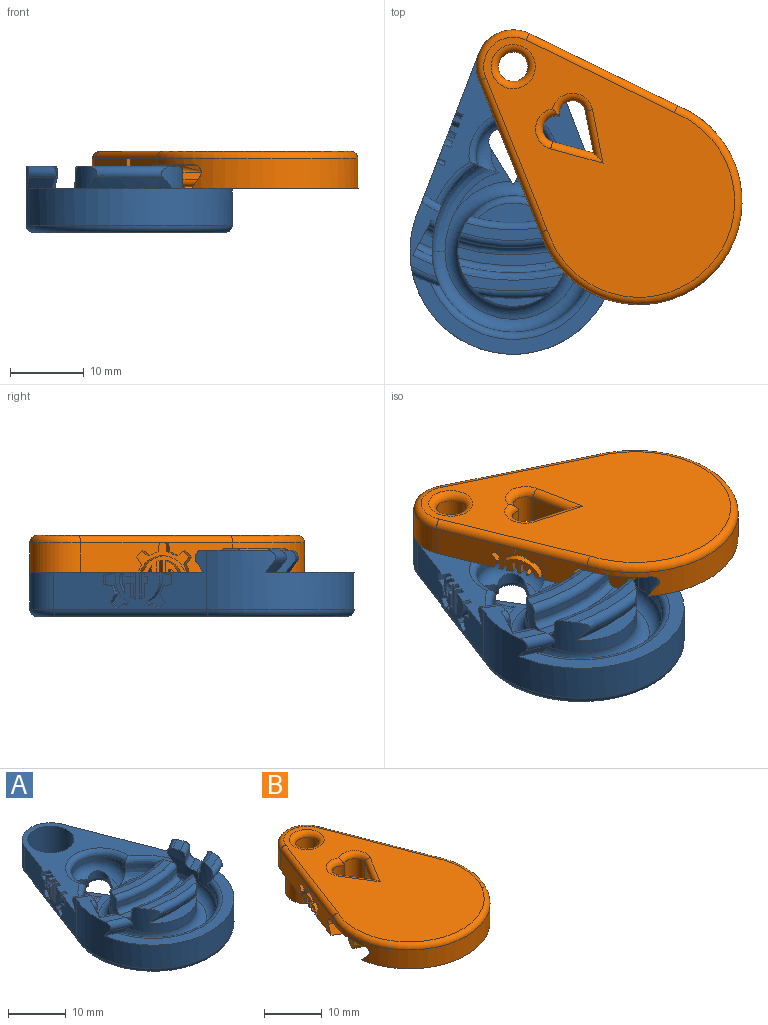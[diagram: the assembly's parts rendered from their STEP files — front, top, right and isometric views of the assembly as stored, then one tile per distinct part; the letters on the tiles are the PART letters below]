
ASSEMBLY  parts=2 mates=1
PART A: 126 faces, bbox 30.3x45.6x9 mm
  f0: plane 24.91x24.4mm, normal (0,0,1), area 152.9mm2, adj f1,f2,f3,f4,f16,f18,f20,f22
  f1: plane 6x5mm, normal (-0.93,0.36,0), area 17.6mm2, adj f0,f32,f88,f89,f90,f93,f95,f96
  f2: plane 8.53x5mm, normal (-0.93,0.36,0), area 40.9mm2, adj f0,f20,f32,f82,f83,f84,f85,f86
  f3: plane 8.01x6.52mm, normal (-0.93,0.36,0), area 34mm2, adj f0,f13,f18,f21,f32,f71,f99,f100
  f4: plane 0.75x0.53mm, normal (-0.93,0.36,0), area 0.4mm2, adj f0,f115,f116,f117
  f5: plane 0.2x0.15mm, normal (0,0,1), area 0mm2, adj f44,f74,f75
  f6: plane 8.32x7.53mm, normal (0,0,1), area 9.5mm2, adj f41,f43,f44,f76
  f7: plane 2.91x2.76mm, normal (0,0,1), area 4mm2, adj f11,f21,f22,f57,f69
  f8: plane 14.14x2.39mm, normal (0,0,1), area 19.7mm2, adj f28,f58,f73
  f9: cylinder r=11mm len=22mm, axis (0,0,-1), area 62.6mm2, adj f10,f11,f12,f13,f14,f15,f39,f42
  f10: extruded ~11.62x6.18mm, area 27.9mm2, adj f9,f13,f18,f25,f36,f41,f52,f53
  f11: extruded ~11.62x6.18mm, area 27.9mm2, adj f7,f9,f16,f25,f38,f45,f49,f50
  f12: plane 3.59x3.19mm, normal (0,0,1), area 5.2mm2, adj f9,f21,f61,f68
  f13: plane 10.21x3.95mm, normal (0,0,1), area 17.1mm2, adj f3,f9,f10,f21,f55,f56,f62,f70
  f14: cone r=32.35mm half-angle=33.7deg, axis (0,0,1), area 7.1mm2, adj f9,f21,f26,f39,f70
  f15: cone r=32.35mm half-angle=33.7deg, axis (0,0,1), area 7.1mm2, adj f9,f21,f26,f39,f68
  f16: cone r=20.36mm half-angle=33.7deg, axis (0,0,-1), area 5.4mm2, adj f0,f11,f22,f38,f69
  f17: plane 13.59x2.23mm, normal (0,0,1), area 18.1mm2, adj f28,f63,f72
  f18: cone r=20.36mm half-angle=33.7deg, axis (0,0,-1), area 5.4mm2, adj f0,f3,f10,f36,f71
  f19: plane 11.06x3.78mm, normal (0,0,1), area 29.3mm2, adj f31,f40
  f20: cylinder r=5mm len=9.34mm, axis (0,0,1), area 60.2mm2, adj f0,f2,f22,f34
  f21: cylinder r=14mm len=28mm, axis (0,0,1), area 324.8mm2, adj f3,f7,f12,f13,f14,f15,f22,f26
  f22: plane 20.87x8.02mm, normal (0.93,0.36,0), area 115.9mm2, adj f0,f7,f16,f20,f21,f35,f69
  f23: cylinder r=4mm len=8mm, axis (0,0,1), area 150.8mm2, adj f0,f24,f34
  f24: plane 39.43x26mm, normal (0,0,-1), area 635.6mm2, adj f23,f32,f33,f35,f78,f79,f80,f81
  f25: cylinder r=5mm len=10mm, axis (0,0,-1), area 18.4mm2, adj f10,f11,f37,f44
  f26: plane 27.74x12.08mm, normal (0,0,1), area 71.8mm2, adj f14,f15,f21,f39
  f27: plane 8.32x7.53mm, normal (0,0,1), area 9.5mm2, adj f43,f44,f45,f77
  f28: cylinder r=7.5mm len=15mm, axis (0,0,-1), area 122.1mm2, adj f8,f17,f29,f30,f31,f40,f43,f46
  f29: plane 11.68x2.8mm, normal (0,0,1), area 18.3mm2, adj f28,f30
  f30: cone r=32.35mm half-angle=33.7deg, axis (0,0,1), area 18.3mm2, adj f28,f29,f72
  f31: cone r=20.36mm half-angle=33.7deg, axis (0,0,-1), area 23.1mm2, adj f19,f28,f40,f73
  f32: cylinder r=1mm len=21.16mm, axis (0.36,0.93,0), area 35mm2, adj f1,f2,f3,f24,f33,f34
  f33: torus R=13mm, axis (0,0,1), area 86.2mm2, adj f21,f24,f32,f35
  f34: torus R=4mm, axis (0,0,1), area 17.5mm2, adj f20,f23,f32,f35
  f35: cylinder r=1mm len=21.26mm, axis (0.36,-0.93,0), area 35.1mm2, adj f22,f24,f33,f34
  f36: bspline ~9.6x7.69mm, area 13.7mm2, adj f0,f10,f18,f37
  f37: torus R=6mm, axis (0,0,1), area 29.8mm2, adj f0,f25,f36,f38
  f38: bspline ~9.6x7.69mm, area 13.7mm2, adj f0,f11,f16,f37
  f39: torus R=12mm, axis (0,0,1), area 46.7mm2, adj f9,f14,f15,f26
  f40: torus R=6.5mm, axis (0,0,1), area 24.3mm2, adj f19,f28,f31
  f41: bspline ~13.9x10.14mm, area 43.7mm2, adj f6,f10,f42,f43,f44
  f42: torus R=9mm, axis (0,0,1), area 94.2mm2, adj f9,f41,f43,f45
  f43: torus R=9.5mm, axis (0,0,1), area 153.4mm2, adj f6,f27,f28,f41,f42,f45,f76,f77
  f44: torus R=3mm, axis (0,0,1), area 45.3mm2, adj f5,f6,f25,f27,f41,f45,f74,f75
  f45: bspline ~13.9x10.14mm, area 43.7mm2, adj f11,f27,f42,f43,f44
  f46: cylinder r=28.06mm len=14.44mm, axis (0,0,-1), area 14.6mm2, adj f28,f63,f65
  f47: cylinder r=24.66mm len=14.68mm, axis (0,0,-1), area 14.9mm2, adj f28,f58,f60
  f48: plane 15x2.51mm, normal (0,0,1), area 21.3mm2, adj f28,f60,f65
  f49: cylinder r=24.66mm len=2.59mm, axis (0,0,-1), area 3mm2, adj f11,f21,f57,f66
  f50: plane 2.99x2.97mm, normal (0,0,1), area 4.4mm2, adj f11,f21,f66,f67
  f51: cylinder r=28.06mm len=3mm, axis (0,0,-1), area 3.4mm2, adj f9,f21,f61,f67
  f52: plane 2.07x1.82mm, normal (0,0,1), area 2.2mm2, adj f10,f55,f59,f64
  f53: cylinder r=24.66mm len=1mm, axis (0,0,-1), area 1mm2, adj f10,f55,f56,f59
  f54: cylinder r=28.06mm len=2.2mm, axis (0,0,-1), area 2.4mm2, adj f9,f55,f62,f64
  f55: plane 4.77x3mm, normal (0.88,-0.47,0), area 10.2mm2, adj f13,f52,f53,f54,f56,f59,f62,f64
  f56: torus R=23.66mm, axis (0,0,1), area 1.3mm2, adj f10,f13,f53,f55
  f57: torus R=23.66mm, axis (0,0,1), area 4.6mm2, adj f7,f11,f21,f49
  f58: torus R=23.66mm, axis (0,0,1), area 23.1mm2, adj f8,f28,f47
  f59: torus R=25.66mm, axis (0,0,1), area 1.8mm2, adj f10,f52,f53,f55
  f60: torus R=25.66mm, axis (0,0,1), area 23.5mm2, adj f28,f47,f48
  f61: torus R=29.06mm, axis (0,0,1), area 5.4mm2, adj f9,f12,f21,f51
  f62: torus R=29.06mm, axis (0,0,1), area 4.3mm2, adj f9,f13,f54,f55
  f63: torus R=29.06mm, axis (0,0,1), area 22.2mm2, adj f17,f28,f46
  f64: torus R=27.06mm, axis (0,0,1), area 3.5mm2, adj f9,f10,f52,f54,f55
  f65: torus R=27.06mm, axis (0,0,1), area 23.4mm2, adj f28,f46,f48
  f66: torus R=25.66mm, axis (0,0,1), area 4.7mm2, adj f11,f21,f49,f50
  f67: torus R=27.06mm, axis (0,0,1), area 5.2mm2, adj f9,f11,f21,f50,f51
  f68: torus R=30.49mm, axis (0,0,1), area 8.5mm2, adj f9,f12,f15,f21
  f69: torus R=22.23mm, axis (0,0,1), area 6mm2, adj f7,f11,f16,f22
  f70: torus R=30.49mm, axis (0,0,1), area 8.5mm2, adj f9,f13,f14,f21
  f71: torus R=22.23mm, axis (0,0,1), area 5.9mm2, adj f3,f10,f13,f18
  f72: torus R=30.49mm, axis (0,0,1), area 20.7mm2, adj f17,f28,f30
  f73: torus R=22.23mm, axis (0,0,1), area 26.4mm2, adj f8,f28,f31
  f74: cylinder r=1.78mm len=3.3mm, axis (0,0,1), area 6.8mm2, adj f5,f44,f75,f77,f79
  f75: cylinder r=1.78mm len=3.3mm, axis (0,0,1), area 6.8mm2, adj f5,f44,f74,f76,f81
  f76: plane 4.91x3.04mm, normal (0.85,0.53,0), area 5.8mm2, adj f6,f43,f44,f75,f77,f80
  f77: plane 4.91x3.04mm, normal (-0.85,0.53,0), area 5.8mm2, adj f27,f43,f44,f74,f76,f78
  f78: cylinder r=1mm len=6.81mm, axis (0.53,0.85,0), area 10.3mm2, adj f24,f77,f79,f80
  f79: torus R=2.78mm, axis (0,0,1), area 9.8mm2, adj f24,f74,f78,f81
  f80: cylinder r=1mm len=6.81mm, axis (0.53,-0.85,0), area 10.3mm2, adj f24,f76,f78,f81
  f81: torus R=2.78mm, axis (0,0,1), area 9.8mm2, adj f24,f75,f79,f80
  f82: plane 1.2x1.06mm, normal (-0.29,-0.75,-0.6), area 1.3mm2, adj f2,f83,f91,f94
  f83: cylinder r=3.85mm len=1.21mm, axis (-0.93,0.36,0), area 1.3mm2, adj f2,f82,f84,f91
  f84: plane 0.93x0.36mm, normal (-0.11,-0.29,0.95), area 0mm2, adj f2,f83,f85,f91
  f85: plane 1.52x1.38mm, normal (-0.05,-0.13,0.99), area 1.3mm2, adj f2,f84,f86,f91
  f86: plane 1.33x0.93mm, normal (-0.36,-0.93,0), area 1.3mm2, adj f2,f85,f87,f91
  f87: plane 1.52x1.38mm, normal (-0.05,-0.13,-0.99), area 1.3mm2, adj f2,f86,f91,f92
  f88: plane 1.03x0.61mm, normal (0.32,0.85,0.42), area 0.6mm2, adj f1,f89,f90,f91
  f89: cylinder r=3.85mm len=1.09mm, axis (-0.93,0.36,0), area 0.5mm2, adj f1,f88,f91,f93
  f90: cylinder r=3.21mm len=3.9mm, axis (-0.93,0.36,0), area 4.7mm2, adj f0,f1,f88,f91
  f91: plane 5x3.4mm, normal (-0.93,0.36,0), area 6.7mm2, adj f0,f82,f83,f84,f85,f86,f87,f88
  f92: cylinder r=3.85mm len=0.95mm, axis (-0.93,0.36,0), area 0.2mm2, adj f0,f2,f87,f91
  f93: plane 1.3x1.29mm, normal (0.21,0.56,0.8), area 1.3mm2, adj f1,f89,f91,f94
  f94: plane 1.27x1.24mm, normal (-0.25,-0.66,0.71), area 1.3mm2, adj f2,f82,f91,f93
  f95: cylinder r=3.21mm len=3.9mm, axis (-0.93,0.36,0), area 4.7mm2, adj f0,f1,f96,f106
  f96: plane 1.03x0.61mm, normal (-0.32,-0.84,0.43), area 0.6mm2, adj f1,f95,f97,f106
  f97: cylinder r=3.85mm len=1.09mm, axis (-0.93,0.36,0), area 0.5mm2, adj f1,f96,f98,f106
  f98: plane 1.3x1.3mm, normal (-0.21,-0.56,0.8), area 1.3mm2, adj f1,f97,f99,f106
  f99: plane 1.27x1.24mm, normal (0.25,0.66,0.71), area 1.3mm2, adj f3,f98,f100,f106
  f100: plane 1.2x1.06mm, normal (0.29,0.75,-0.6), area 1.3mm2, adj f3,f99,f101,f106
  f101: cylinder r=3.85mm len=1.21mm, axis (-0.93,0.36,0), area 1.3mm2, adj f3,f100,f102,f106
  f102: plane 1.52x1.38mm, normal (0.05,0.13,0.99), area 1.3mm2, adj f3,f101,f103,f106
  f103: plane 1.33x0.93mm, normal (0.36,0.93,0), area 1.3mm2, adj f3,f102,f104,f106
  f104: plane 1.52x1.38mm, normal (0.05,0.13,-0.99), area 1.3mm2, adj f3,f103,f105,f106
  f105: cylinder r=3.85mm len=0.95mm, axis (-0.93,0.36,0), area 0.2mm2, adj f0,f3,f104,f106
  f106: plane 5x3.4mm, normal (-0.93,0.36,0), area 6.7mm2, adj f0,f95,f96,f97,f98,f99,f100,f101
  f107: plane 1.1x0.79mm, normal (0,0,-1), area 0.5mm2, adj f1,f108,f113,f114
  f108: plane 0.93x0.53mm, normal (0.36,0.93,0), area 0.5mm2, adj f0,f1,f107,f114
  f109: plane 3.64x0.93mm, normal (-0.36,-0.93,0), area 3.6mm2, adj f0,f1,f110,f114
  f110: cylinder r=2.65mm len=1.22mm, axis (-0.93,0.36,0), area 0.8mm2, adj f1,f109,f111,f114
  f111: plane 1.99x0.93mm, normal (0.36,0.93,0), area 2mm2, adj f1,f110,f112,f114
  f112: plane 1.1x0.79mm, normal (0,0,1), area 0.5mm2, adj f1,f111,f113,f114
  f113: plane 0.93x0.92mm, normal (0.36,0.93,0), area 0.9mm2, adj f1,f107,f112,f114
  f114: plane 3.64x1.17mm, normal (-0.93,0.36,0), area 3.3mm2, adj f0,f107,f108,f109,f110,f111,f112,f113
  f115: plane 0.93x0.53mm, normal (-0.36,-0.93,0), area 0.5mm2, adj f0,f4,f116,f125
  f116: plane 1.22x1.11mm, normal (0,0,-1), area 0.8mm2, adj f4,f115,f117,f125
  f117: plane 0.93x0.53mm, normal (0.36,0.93,0), area 0.5mm2, adj f0,f4,f116,f125
  f118: cylinder r=2.63mm len=2.88mm, axis (-0.93,0.36,0), area 3.1mm2, adj f0,f1,f119,f125
  f119: plane 1.43x0.93mm, normal (0.36,0.93,0), area 1.4mm2, adj f1,f118,f120,f125
  f120: plane 1.22x1.11mm, normal (0,0,1), area 0.8mm2, adj f1,f119,f121,f125
  f121: plane 1.99x0.93mm, normal (-0.36,-0.93,0), area 2mm2, adj f1,f120,f122,f125
  f122: plane 0.93x0.36mm, normal (-0.36,-0.93,0.01), area 0mm2, adj f1,f121,f123,f125
  f123: cylinder r=2.65mm len=1.22mm, axis (-0.93,0.36,0), area 0.8mm2, adj f1,f122,f124,f125
  f124: plane 3.64x0.93mm, normal (0.36,0.93,0), area 3.6mm2, adj f0,f1,f123,f125
  f125: plane 3.64x2.24mm, normal (-0.93,0.36,0), area 5.4mm2, adj f0,f115,f116,f117,f118,f119,f120,f121
PART B: 68 faces, bbox 31.4x45.6x11 mm
  f0: plane 5.7x2.22mm, normal (-0.93,0.36,0), area 5.8mm2, adj f4,f40,f58,f59,f62,f63,f65,f66
  f1: plane 0.43x0.4mm, normal (-0.93,0.36,0), area 0.1mm2, adj f4,f55,f56,f57
  f2: plane 8.76x4.01mm, normal (-0.93,0.36,0), area 24.5mm2, adj f4,f7,f11,f14,f18,f31,f41,f42
  f3: plane 10.76x4.13mm, normal (-0.93,0.36,0), area 38.3mm2, adj f4,f9,f18,f48,f49,f50,f51,f52
  f4: plane 27.04x24.74mm, normal (0,0,-1), area 348.8mm2, adj f0,f1,f2,f3,f9,f10,f14,f16
  f5: cylinder r=27.86mm len=27.05mm, axis (0,0,-1), area 28.2mm2, adj f11,f25,f27,f28
  f6: cylinder r=24.86mm len=25.05mm, axis (0,0,-1), area 26.3mm2, adj f11,f25,f26,f29
  f7: plane 28x12.77mm, normal (0,0,-1), area 119.1mm2, adj f2,f10,f11,f25,f26,f27,f30,f31
  f8: plane 42x26mm, normal (0,0,1), area 657.6mm2, adj f18,f19,f20,f21,f23,f36,f37,f38
  f9: cylinder r=5mm len=9.34mm, axis (0,0,-1), area 48.2mm2, adj f3,f4,f10,f19
  f10: plane 20.87x8.02mm, normal (0.93,0.36,0), area 83.9mm2, adj f4,f7,f9,f11,f14,f21,f31
  f11: cylinder r=14mm len=28mm, axis (0,0,-1), area 174.6mm2, adj f2,f5,f6,f7,f10,f12,f13,f20
  f12: plane 27.65x11.79mm, normal (0,0,-1), area 184.7mm2, adj f11,f13
  f13: cone r=32.73mm half-angle=33.7deg, axis (0,0,1), area 56mm2, adj f11,f12,f30
  f14: cone r=19.99mm half-angle=33.7deg, axis (0,0,-1), area 51.1mm2, adj f2,f4,f10,f31
  f15: cylinder r=2mm len=9mm, axis (0,0,1), area 113.1mm2, adj f22,f23
  f16: cylinder r=3.7mm len=7.4mm, axis (0,0,1), area 139.5mm2, adj f4,f17
  f17: plane 7.4x7.4mm, normal (0,0,-1), area 14.7mm2, adj f16,f22
  f18: cylinder r=1mm len=21.16mm, axis (-0.36,-0.93,0), area 35mm2, adj f2,f3,f8,f19,f20,f47
  f19: torus R=4mm, axis (0,0,1), area 17.5mm2, adj f8,f9,f18,f21
  f20: torus R=13mm, axis (0,0,1), area 86.2mm2, adj f8,f11,f18,f21
  f21: cylinder r=1mm len=21.26mm, axis (-0.36,0.93,0), area 35.1mm2, adj f8,f10,f19,f20
  f22: torus R=3mm, axis (0,0,-1), area 23.3mm2, adj f15,f17
  f23: torus R=3mm, axis (0,0,1), area 23.3mm2, adj f8,f15
  f24: plane 26.46x4.9mm, normal (0,0,-1), area 27.4mm2, adj f11,f25,f28,f29
  f25: plane 4.41x3mm, normal (-0.88,0.47,0), area 9mm2, adj f5,f6,f7,f24,f26,f27,f28,f29
  f26: torus R=23.86mm, axis (0,0,-1), area 40.8mm2, adj f6,f7,f11,f25
  f27: torus R=28.86mm, axis (0,0,-1), area 44.6mm2, adj f5,f7,f11,f25
  f28: torus R=26.86mm, axis (0,0,1), area 44mm2, adj f5,f11,f24,f25
  f29: torus R=25.86mm, axis (0,0,1), area 41.7mm2, adj f6,f11,f24,f25
  f30: torus R=30.86mm, axis (0,0,-1), area 60.5mm2, adj f7,f11,f13
  f31: torus R=21.86mm, axis (0,0,-1), area 55.1mm2, adj f2,f7,f10,f14
  f32: cylinder r=1.78mm len=4mm, axis (0,0,1), area 22.4mm2, adj f4,f33,f35,f37
  f33: cylinder r=1.78mm len=4mm, axis (0,0,1), area 22.4mm2, adj f4,f32,f34,f39
  f34: plane 4.91x4mm, normal (0.85,0.53,0), area 23.1mm2, adj f4,f33,f35,f38
  f35: plane 4.91x4mm, normal (-0.85,0.53,0), area 23.1mm2, adj f4,f32,f34,f36
  f36: cylinder r=1mm len=6.81mm, axis (-0.53,-0.85,0), area 10mm2, adj f8,f35,f37,f38
  f37: torus R=2.78mm, axis (0,0,1), area 9.8mm2, adj f8,f32,f36,f39
  f38: cylinder r=1mm len=6.81mm, axis (-0.53,0.85,0), area 10mm2, adj f8,f34,f36,f39
  f39: torus R=2.78mm, axis (0,0,1), area 9.8mm2, adj f8,f33,f37,f38
  f40: cylinder r=3.21mm len=6.06mm, axis (-0.93,0.36,0), area 8.1mm2, adj f0,f4,f54
  f41: cylinder r=3.85mm len=1.1mm, axis (-0.93,0.36,0), area 1.2mm2, adj f2,f4,f42,f54
  f42: plane 1.2x1.06mm, normal (0.29,0.75,0.6), area 1.3mm2, adj f2,f41,f43,f54
  f43: plane 1.27x1.24mm, normal (0.25,0.66,-0.71), area 1.3mm2, adj f2,f42,f44,f54
  f44: plane 1.3x1.3mm, normal (-0.21,-0.56,-0.8), area 1.3mm2, adj f2,f43,f45,f54
  f45: cylinder r=3.85mm len=1.49mm, axis (-0.93,0.36,0), area 1.3mm2, adj f2,f44,f46,f54
  f46: plane 1.24x1mm, normal (0.35,0.92,-0.14), area 1.3mm2, adj f2,f45,f47,f54
  f47: plane 1.61x1.41mm, normal (0,0,-1), area 1.3mm2, adj f18,f46,f48,f54
  f48: plane 1.24x1mm, normal (-0.35,-0.92,-0.14), area 1.3mm2, adj f3,f47,f49,f54
  f49: cylinder r=3.85mm len=1.49mm, axis (-0.93,0.36,0), area 1.3mm2, adj f3,f48,f50,f54
  f50: plane 1.3x1.3mm, normal (0.21,0.56,-0.8), area 1.3mm2, adj f3,f49,f51,f54
  f51: plane 1.27x1.24mm, normal (-0.25,-0.66,-0.71), area 1.3mm2, adj f3,f50,f52,f54
  f52: plane 1.2x1.06mm, normal (-0.29,-0.75,0.6), area 1.3mm2, adj f3,f51,f53,f54
  f53: cylinder r=3.85mm len=1.1mm, axis (-0.93,0.36,0), area 1.2mm2, adj f3,f4,f52,f54
  f54: plane 7.48x4mm, normal (-0.93,0.36,0), area 11.1mm2, adj f4,f40,f41,f42,f43,f44,f45,f46
  f55: plane 0.93x0.43mm, normal (0.36,0.93,0), area 0.4mm2, adj f1,f4,f56,f60
  f56: plane 0.94x0.37mm, normal (-0.17,-0.44,0.88), area 0mm2, adj f1,f55,f57,f60
  f57: cylinder r=1.76mm len=1.08mm, axis (-0.93,0.36,0), area 0.6mm2, adj f1,f4,f56,f60
  f58: cylinder r=2.65mm len=2.44mm, axis (-0.93,0.36,0), area 2.9mm2, adj f0,f4,f59,f60
  f59: plane 1.65x0.93mm, normal (-0.36,-0.93,0), area 1.7mm2, adj f0,f4,f58,f60
  f60: plane 2.08x1.65mm, normal (-0.93,0.36,0), area 2.5mm2, adj f4,f55,f56,f57,f58,f59
  f61: plane 0.9x0.57mm, normal (-0.93,0.36,0), area 0.3mm2, adj f4,f62,f63
  f62: cylinder r=2.63mm len=1.15mm, axis (-0.93,0.36,0), area 1.1mm2, adj f0,f4,f61,f63
  f63: plane 0.93x0.9mm, normal (0.36,0.93,0), area 0.9mm2, adj f0,f4,f61,f62
  f64: plane 1.65x0.75mm, normal (-0.93,0.36,0), area 1.3mm2, adj f4,f65,f66,f67
  f65: plane 1.45x0.93mm, normal (-0.36,-0.93,0), area 1.5mm2, adj f0,f4,f64,f67
  f66: plane 1.65x0.93mm, normal (0.36,0.93,0), area 1.7mm2, adj f0,f4,f64,f67
  f67: cylinder r=2.65mm len=1.22mm, axis (-0.93,0.36,0), area 0.8mm2, adj f0,f64,f65,f66
PLACE A t=(-17.33,-5.72,1.09)mm
PLACE B rot(axis=(0,0,1),43deg) t=(-0.28,0.99,1.09)mm
MATE revolute B.f9 <-> A.f23  axis (0,0,-1) through (-17.33,19.28,-0.91)mm
